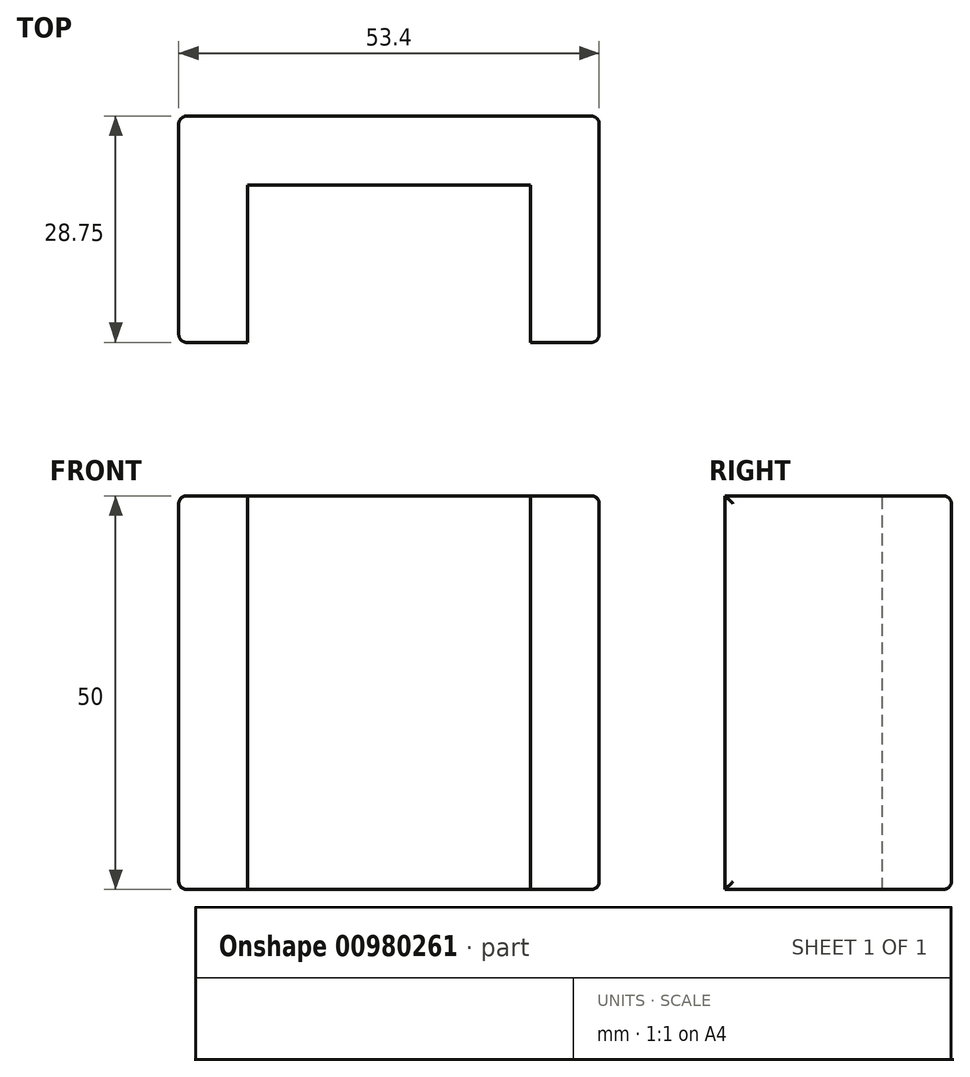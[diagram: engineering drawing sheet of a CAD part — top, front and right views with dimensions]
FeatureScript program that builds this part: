
annotation { "Feature Type Name" : "Feature", "Feature Type Description" : "" }
export const myFeature = defineFeature(function(context is Context, id is Id, definition is map)
    precondition{}
    {
        {
            var Q0;
            Q0=qCreatedBy(makeId("Top.planeOp"),FACE);
            var sketch = newSketch(context, id + "F0", { "sketchPlane" : qUnion([Q0])});
            skLineSegment(sketch, "E0", {"start": v(0, 0) * mm, "end": v(0, 20) * mm});
            skLineSegment(sketch, "E1", {"start": v(0, 20) * mm, "end": v(35.9, 20) * mm});
            skLineSegment(sketch, "E2", {"start": v(35.9, 20) * mm, "end": v(35.9, 0) * mm});
            skLineSegment(sketch, "E3.0", {"start": v(44.65, 28.75) * mm, "end": v(44.65, 0) * mm});
            skLineSegment(sketch, "E3.1", {"start": v(-8.75, 28.75) * mm, "end": v(44.65, 28.75) * mm});
            skLineSegment(sketch, "E3.2", {"start": v(-8.75, 0) * mm, "end": v(-8.75, 28.75) * mm});
            skLineSegment(sketch, "E4", {"start": v(-8.75, 0) * mm, "end": v(0, 0) * mm});
            skLineSegment(sketch, "E5", {"start": v(35.9, 0) * mm, "end": v(44.65, 0) * mm});
            skSolve(sketch);
        }
        {
            var Q0;
            Q0=qSketchRegion(id+"F0",true);
            extrude(context, id + "F1", {"entities" : qUnion([Q0]), "oppositeDirection" : true, "depth" : 50 * mm, "offsetDistance" : 25 * mm});
        }
        {
            var Q0;
            Q0=makeQuery(id+"F1.opExtrude","SWEPT_FACE",FACE,{"disambiguationData":[OSD([sQuery(id+"F0.wireOp",EDGE,"E3.1")])]});
            var Q1;
            Q1=makeQuery(id+"F1.opExtrude","SWEPT_FACE",FACE,{"disambiguationData":[OSD([sQuery(id+"F0.wireOp",EDGE,"E3.2")])]});
            var Q2;
            Q2=makeQuery(id+"F1.opExtrude","SWEPT_FACE",FACE,{"disambiguationData":[OSD([sQuery(id+"F0.wireOp",EDGE,"E3.0")])]});
            fillet(context, id + "F2", {"entities" : qUnion([Q0, Q1, Q2]), "radius" : 1 * mm, "tangentPropagation" : true, "allowEdgeOverflow" : false});
        }
    });
